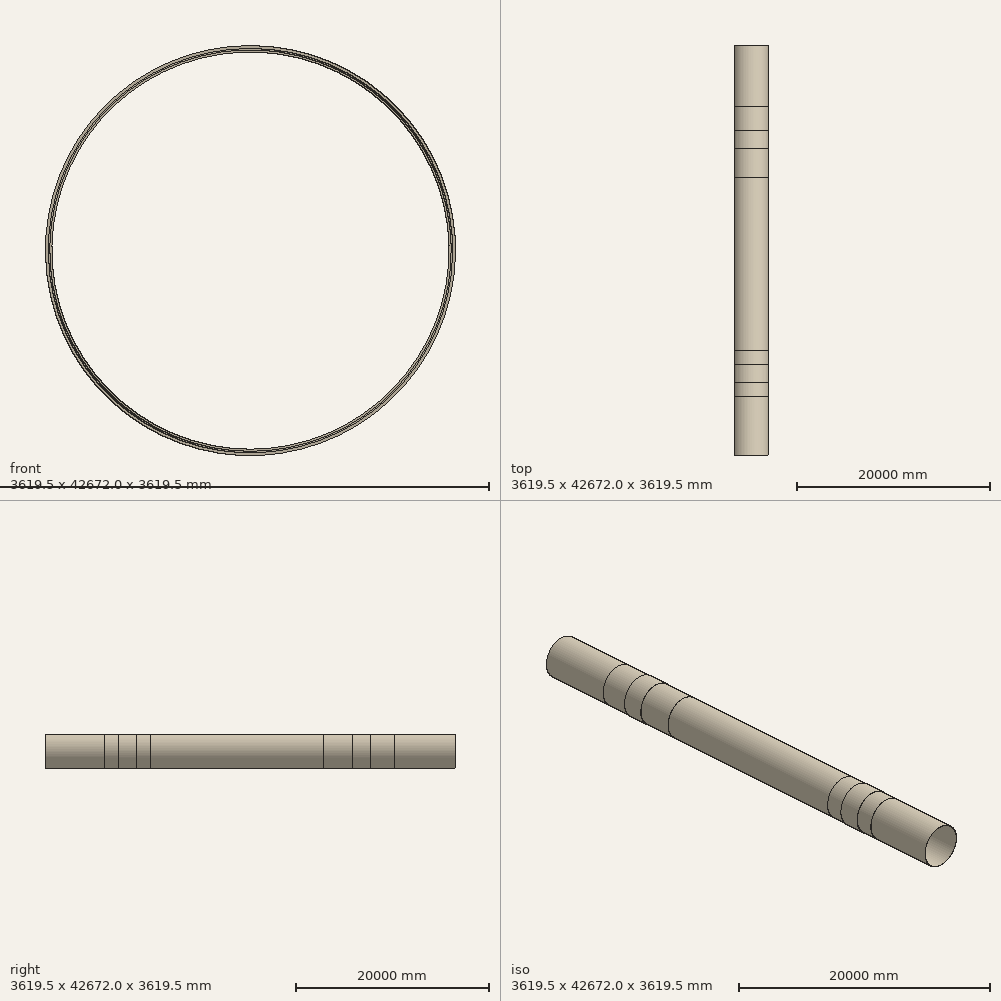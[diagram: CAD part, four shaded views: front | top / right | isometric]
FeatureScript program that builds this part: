
annotation { "Feature Type Name" : "Feature", "Feature Type Description" : "" }
export const myFeature = defineFeature(function(context is Context, id is Id, definition is map)
    precondition{}
    {
        {
            var Q0;
            Q0=qCreatedBy(makeId("Front.planeOp"),FACE);
            var sketch = newSketch(context, id + "F0", { "sketchPlane" : qUnion([Q0])});
            skCircle(sketch, "E0", {"center": v(0, 0) * mm, "radius": 1752.6 * mm});
            skCircle(sketch, "E1", {"center": v(0, 0) * mm, "radius": 1771.65 * mm});
            skSolve(sketch);
        }
        {
            var Q0;
            Q0=makeQuery(id+"F0.imprint","IMPRINT",FACE,{"disambiguationData":[TD([[makeQuery(id+"F0.imprint","IMPRINT",EDGE,{"derivedFrom":sQuery(id+"F0.wireOp",EDGE,"E0")}),-1.0]])]});
            extrude(context, id + "F1", {"entities" : qUnion([Q0]), "depth" : 6096 * mm});
        }
        {
            var Q0;
            Q0=makeQuery(id+"F1.opExtrude","CAP_FACE",FACE,{"disambiguationData":[OSD([sQuery(id+"F0.wireOp",EDGE,"E0"),sQuery(id+"F0.wireOp",EDGE,"E1")])],"isStart":true});
            var sketch = newSketch(context, id + "F2", { "sketchPlane" : qUnion([Q0])});
            skCircle(sketch, "E2.0", {"center": v(0, 0) * mm, "radius": 1784.35 * mm});
            skSolve(sketch);
        }
        {
            var Q0;
            Q0=makeQuery(id+"F2.imprint","IMPRINT",FACE,{"disambiguationData":[TD([[makeQuery(id+"F2.imprint","IMPRINT",EDGE,{"derivedFrom":sQuery(id+"F2.wireOp",EDGE,"E2.0")}),1.0]])]});
            var Q1;
            Q1=makeQuery(id+"F2.imprint","IMPRINT",FACE,{"disambiguationData":[TD([[makeQuery(id+"F2.imprint","IMPRINT",EDGE,{"derivedFrom":makeQuery(id+"F1.opExtrude","CAP_EDGE",EDGE,{"disambiguationData":[OSD([sQuery(id+"F0.wireOp",EDGE,"E0")])],"isStart":true})}),1.0]])]});
            extrude(context, id + "F3", {"entities" : qUnion([Q0, Q1]), "operationType" : NewBodyOperationType.ADD, "depth" : 1524 * mm});
        }
        {
            var Q0;
            Q0=makeQuery(id+"F3.opExtrude","CAP_FACE",FACE,{"disambiguationData":[OSD([sQuery(id+"F0.wireOp",EDGE,"E0"),sQuery(id+"F2.wireOp",EDGE,"E2.0")])],"isStart":false});
            var sketch = newSketch(context, id + "F4", { "sketchPlane" : qUnion([Q0])});
            skCircle(sketch, "E3.0", {"center": v(0, 0) * mm, "radius": 1809.75 * mm});
            skSolve(sketch);
        }
        {
            var Q0;
            Q0=makeQuery(id+"F4.imprint","IMPRINT",FACE,{"disambiguationData":[TD([[makeQuery(id+"F4.imprint","IMPRINT",EDGE,{"derivedFrom":sQuery(id+"F4.wireOp",EDGE,"E3.0")}),1.0]])]});
            var Q1;
            Q1=makeQuery(id+"F4.imprint","IMPRINT",FACE,{"disambiguationData":[TD([[makeQuery(id+"F4.imprint","IMPRINT",EDGE,{"derivedFrom":makeQuery(id+"F3.opExtrude","CAP_EDGE",EDGE,{"disambiguationData":[OSD([sQuery(id+"F2.wireOp",EDGE,"E2.0")])],"isStart":false})}),1.0]])]});
            extrude(context, id + "F5", {"entities" : qUnion([Q0, Q1]), "operationType" : NewBodyOperationType.ADD, "depth" : 1828.8 * mm});
        }
        {
            var Q0;
            Q0=makeQuery(id+"F5.opExtrude","CAP_FACE",FACE,{"disambiguationData":[OSD([sQuery(id+"F0.wireOp",EDGE,"E0"),sQuery(id+"F4.wireOp",EDGE,"E3.0")])],"isStart":false});
            var sketch = newSketch(context, id + "F6", { "sketchPlane" : qUnion([Q0])});
            skCircle(sketch, "E4.0", {"center": v(0, 0) * mm, "radius": 1784.35 * mm});
            skSolve(sketch);
        }
        {
            var Q0;
            Q0=makeQuery(id+"F6.imprint","IMPRINT",FACE,{"disambiguationData":[TD([[makeQuery(id+"F6.imprint","IMPRINT",EDGE,{"derivedFrom":sQuery(id+"F6.wireOp",EDGE,"E4.0")}),1.0]])]});
            extrude(context, id + "F7", {"entities" : qUnion([Q0]), "operationType" : NewBodyOperationType.ADD, "depth" : 1524 * mm});
        }
        {
            var Q0;
            Q0=makeQuery(id+"F7.opExtrude","CAP_FACE",FACE,{"disambiguationData":[OSD([sQuery(id+"F0.wireOp",EDGE,"E0"),sQuery(id+"F6.wireOp",EDGE,"E4.0")])],"isStart":false});
            var sketch = newSketch(context, id + "F8", { "sketchPlane" : qUnion([Q0])});
            skCircle(sketch, "E5.0", {"center": v(0, 0) * mm, "radius": 1771.65 * mm});
            skSolve(sketch);
        }
        {
            var Q0;
            Q0=makeQuery(id+"F8.imprint","IMPRINT",FACE,{"disambiguationData":[TD([[makeQuery(id+"F8.imprint","IMPRINT",EDGE,{"derivedFrom":sQuery(id+"F8.wireOp",EDGE,"E5.0")}),1.0]])]});
            extrude(context, id + "F9", {"entities" : qUnion([Q0]), "operationType" : NewBodyOperationType.ADD, "depth" : 17983.2 * mm});
        }
        {
            var Q0;
            Q0=makeQuery(id+"F9.opExtrude","CAP_FACE",FACE,{"disambiguationData":[OSD([sQuery(id+"F0.wireOp",EDGE,"E0"),sQuery(id+"F8.wireOp",EDGE,"E5.0")])],"isStart":false});
            var sketch = newSketch(context, id + "F10", { "sketchPlane" : qUnion([Q0])});
            skCircle(sketch, "E6.0", {"center": v(0, 0) * mm, "radius": 1784.35 * mm});
            skSolve(sketch);
        }
        {
            var Q0;
            Q0=makeQuery(id+"F10.imprint","IMPRINT",FACE,{"disambiguationData":[TD([[makeQuery(id+"F10.imprint","IMPRINT",EDGE,{"derivedFrom":sQuery(id+"F10.wireOp",EDGE,"E6.0")}),1.0]])]});
            var Q1;
            Q1=makeQuery(id+"F10.imprint","IMPRINT",FACE,{"disambiguationData":[TD([[makeQuery(id+"F10.imprint","IMPRINT",EDGE,{"derivedFrom":makeQuery(id+"F9.opExtrude","CAP_EDGE",EDGE,{"disambiguationData":[OSD([sQuery(id+"F8.wireOp",EDGE,"E5.0")])],"isStart":false})}),1.0]])]});
            extrude(context, id + "F11", {"entities" : qUnion([Q0, Q1]), "operationType" : NewBodyOperationType.ADD, "depth" : 3048 * mm});
        }
        {
            var Q0;
            Q0=makeQuery(id+"F11.opExtrude","CAP_FACE",FACE,{"disambiguationData":[OSD([sQuery(id+"F0.wireOp",EDGE,"E0"),sQuery(id+"F10.wireOp",EDGE,"E6.0")])],"isStart":false});
            var sketch = newSketch(context, id + "F12", { "sketchPlane" : qUnion([Q0])});
            skCircle(sketch, "E7.0", {"center": v(0, 0) * mm, "radius": 1809.75 * mm});
            skSolve(sketch);
        }
        {
            var Q0;
            Q0=makeQuery(id+"F12.imprint","IMPRINT",FACE,{"disambiguationData":[TD([[makeQuery(id+"F12.imprint","IMPRINT",EDGE,{"derivedFrom":sQuery(id+"F12.wireOp",EDGE,"E7.0")}),1.0]])]});
            var Q1;
            Q1=makeQuery(id+"F12.imprint","IMPRINT",FACE,{"disambiguationData":[TD([[makeQuery(id+"F12.imprint","IMPRINT",EDGE,{"derivedFrom":makeQuery(id+"F11.opExtrude","CAP_EDGE",EDGE,{"disambiguationData":[OSD([sQuery(id+"F10.wireOp",EDGE,"E6.0")])],"isStart":false})}),1.0]])]});
            extrude(context, id + "F13", {"entities" : qUnion([Q0, Q1]), "operationType" : NewBodyOperationType.ADD, "depth" : 1828.8 * mm});
        }
        {
            var Q0;
            Q0=makeQuery(id+"F13.opExtrude","CAP_FACE",FACE,{"disambiguationData":[OSD([sQuery(id+"F0.wireOp",EDGE,"E0"),sQuery(id+"F12.wireOp",EDGE,"E7.0")])],"isStart":false});
            var sketch = newSketch(context, id + "F14", { "sketchPlane" : qUnion([Q0])});
            skCircle(sketch, "E8.0", {"center": v(0, 0) * mm, "radius": 1784.35 * mm});
            skSolve(sketch);
        }
        {
            var Q0;
            Q0=makeQuery(id+"F14.imprint","IMPRINT",FACE,{"disambiguationData":[TD([[makeQuery(id+"F14.imprint","IMPRINT",EDGE,{"derivedFrom":sQuery(id+"F14.wireOp",EDGE,"E8.0")}),1.0]])]});
            extrude(context, id + "F15", {"entities" : qUnion([Q0]), "operationType" : NewBodyOperationType.ADD, "depth" : 2438.4 * mm});
        }
        {
            var Q0;
            Q0=makeQuery(id+"F15.opExtrude","CAP_FACE",FACE,{"disambiguationData":[OSD([sQuery(id+"F0.wireOp",EDGE,"E0"),sQuery(id+"F14.wireOp",EDGE,"E8.0")])],"isStart":false});
            var sketch = newSketch(context, id + "F16", { "sketchPlane" : qUnion([Q0])});
            skCircle(sketch, "E9.0", {"center": v(0, 0) * mm, "radius": 1771.65 * mm});
            skSolve(sketch);
        }
        {
            var Q0;
            Q0=makeQuery(id+"F16.imprint","IMPRINT",FACE,{"disambiguationData":[TD([[makeQuery(id+"F16.imprint","IMPRINT",EDGE,{"derivedFrom":sQuery(id+"F16.wireOp",EDGE,"E9.0")}),1.0]])]});
            extrude(context, id + "F17", {"entities" : qUnion([Q0]), "operationType" : NewBodyOperationType.ADD, "depth" : 6400.8 * mm});
        }
    });
